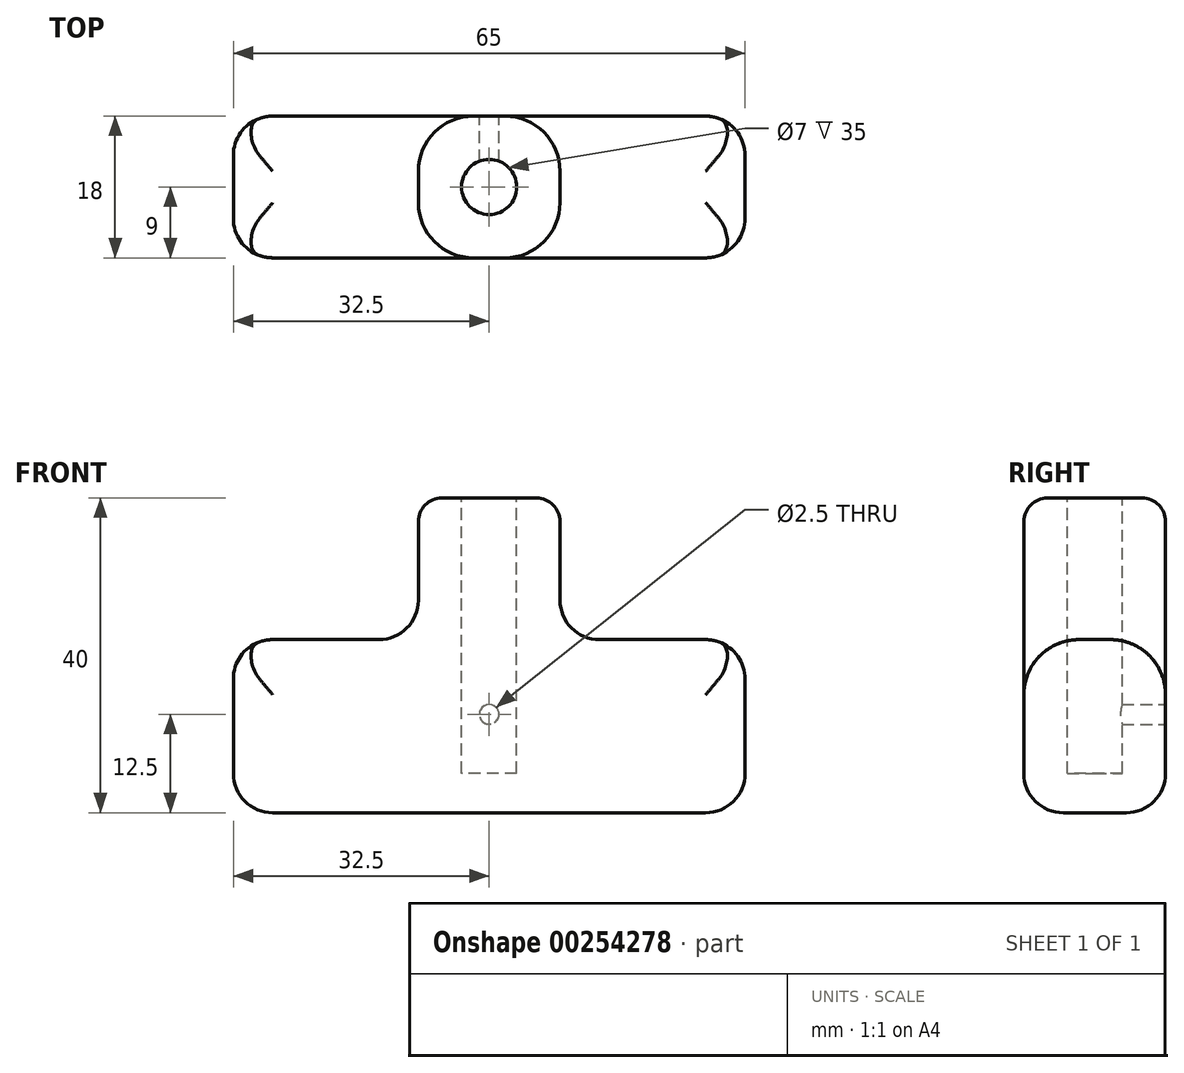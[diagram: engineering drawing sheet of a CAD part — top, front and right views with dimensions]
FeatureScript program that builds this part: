
annotation { "Feature Type Name" : "Feature", "Feature Type Description" : "" }
export const myFeature = defineFeature(function(context is Context, id is Id, definition is map)
    precondition{}
    {
        {
            var Q0;
            Q0=qCreatedBy(makeId("Front.planeOp"),FACE);
            var sketch = newSketch(context, id + "F0", { "sketchPlane" : qUnion([Q0])});
            skLineSegment(sketch, "E0", {"start": v(0, 0) * mm, "end": v(0, 40) * mm, "construction": true});
            skLineSegment(sketch, "E1", {"start": v(0, 0) * mm, "end": v(32.5, 0) * mm});
            skLineSegment(sketch, "E2", {"start": v(32.5, 0) * mm, "end": v(32.5, 22) * mm});
            skLineSegment(sketch, "E3", {"start": v(32.5, 22) * mm, "end": v(9, 22) * mm});
            skLineSegment(sketch, "E4", {"start": v(9, 22) * mm, "end": v(9, 40) * mm});
            skLineSegment(sketch, "E5", {"start": v(9, 40) * mm, "end": v(0, 40) * mm});
            skLineSegment(sketch, "E6.MirrorCS", {"start": v(-9, 40) * mm, "end": v(0, 40) * mm});
            skLineSegment(sketch, "E7.MirrorCS", {"start": v(-9, 22) * mm, "end": v(-9, 40) * mm});
            skLineSegment(sketch, "E8.MirrorCS", {"start": v(-32.5, 22) * mm, "end": v(-9, 22) * mm});
            skLineSegment(sketch, "E9.MirrorCS", {"start": v(-32.5, 0) * mm, "end": v(-32.5, 22) * mm});
            skLineSegment(sketch, "E10.MirrorCS", {"start": v(0, 0) * mm, "end": v(-32.5, 0) * mm});
            skSolve(sketch);
        }
        {
            var Q0;
            Q0=makeQuery(id+"F0.imprint","IMPRINT",FACE,{"disambiguationData":[TD([[makeQuery(id+"F0.imprint","IMPRINT",EDGE,{"derivedFrom":sQuery(id+"F0.wireOp",EDGE,"E1")}),1.0]])]});
            extrude(context, id + "F1", {"entities" : qUnion([Q0]), "depth" : 18 * mm, "offsetDistance" : 25 * mm, "symmetric" : true});
        }
        {
            var Q0;
            Q0=makeQuery(id+"F1.opExtrude","SWEPT_FACE",FACE,{"disambiguationData":[OSD([sQuery(id+"F0.wireOp",EDGE,"E5"),sQuery(id+"F0.wireOp",EDGE,"E6.MirrorCS")])]});
            var sketch = newSketch(context, id + "F2", { "sketchPlane" : qUnion([Q0])});
            skPoint(sketch, "E11.0", {"position": v(0, 0) * mm});
            skCircle(sketch, "E12", {"center": v(0, 0) * mm, "radius": 3.5 * mm});
            skSolve(sketch);
        }
        {
            var Q0;
            Q0=makeQuery(id+"F2.imprint","IMPRINT",FACE,{"disambiguationData":[TD([[makeQuery(id+"F2.imprint","IMPRINT",EDGE,{"derivedFrom":sQuery(id+"F2.wireOp",EDGE,"E12")}),1.0]])]});
            extrude(context, id + "F3", {"entities" : qUnion([Q0]), "operationType" : NewBodyOperationType.REMOVE, "oppositeDirection" : true, "depth" : 35 * mm, "offsetDistance" : 25 * mm});
        }
        {
            var Q0;
            Q0=makeQuery(id+"F1.opExtrude","CAP_EDGE",EDGE,{"disambiguationData":[OSD([sQuery(id+"F0.wireOp",EDGE,"E8.MirrorCS")])],"isStart":false});
            var Q1;
            Q1=makeQuery(id+"F1.opExtrude","CAP_EDGE",EDGE,{"disambiguationData":[OSD([sQuery(id+"F0.wireOp",EDGE,"E8.MirrorCS")])],"isStart":true});
            var Q2;
            Q2=makeQuery(id+"F1.opExtrude","CAP_EDGE",EDGE,{"disambiguationData":[OSD([sQuery(id+"F0.wireOp",EDGE,"E3")])],"isStart":false});
            var Q3;
            Q3=makeQuery(id+"F1.opExtrude","CAP_EDGE",EDGE,{"disambiguationData":[OSD([sQuery(id+"F0.wireOp",EDGE,"E3")])],"isStart":true});
            var Q4;
            Q4=makeQuery(id+"F1.opExtrude","CAP_EDGE",EDGE,{"disambiguationData":[OSD([sQuery(id+"F0.wireOp",EDGE,"E1"),sQuery(id+"F0.wireOp",EDGE,"E10.MirrorCS")])],"isStart":false});
            var Q5;
            Q5=makeQuery(id+"F1.opExtrude","CAP_EDGE",EDGE,{"disambiguationData":[OSD([sQuery(id+"F0.wireOp",EDGE,"E1"),sQuery(id+"F0.wireOp",EDGE,"E10.MirrorCS")])],"isStart":true});
            fillet(context, id + "F4", {"entities" : qUnion([Q0, Q1, Q2, Q3, Q4, Q5]), "tangentPropagation" : true, "radius" : 5 * mm, "defaultsChanged" : true, "vertexSettings" : [], "allowEdgeOverflow" : false});
        }
        {
            var Q0;
            Q0=makeQuery(id+"F1.opExtrude","CAP_EDGE",EDGE,{"disambiguationData":[OSD([sQuery(id+"F0.wireOp",EDGE,"E9.MirrorCS")])],"isStart":true});
            var Q1;
            Q1=makeQuery(id+"F1.opExtrude","CAP_EDGE",EDGE,{"disambiguationData":[OSD([sQuery(id+"F0.wireOp",EDGE,"E2")])],"isStart":true});
            var Q2;
            Q2=makeQuery(id+"F1.opExtrude","SWEPT_EDGE",EDGE,{"disambiguationData":[OSD([sQuery(id+"F0.wireOp",EDGE,"E3"),sQuery(id+"F0.wireOp",EDGE,"E4")])]});
            var Q3;
            Q3=makeQuery(id+"F1.opExtrude","SWEPT_EDGE",EDGE,{"disambiguationData":[OSD([sQuery(id+"F0.wireOp",EDGE,"E7.MirrorCS"),sQuery(id+"F0.wireOp",EDGE,"E8.MirrorCS")])]});
            fillet(context, id + "F5", {"entities" : qUnion([Q0, Q1, Q2, Q3]), "tangentPropagation" : true, "radius" : 5 * mm, "defaultsChanged" : false, "vertexSettings" : [], "allowEdgeOverflow" : false});
        }
        {
            var Q0;
            Q0=makeQuery(id+"F1.opExtrude","CAP_EDGE",EDGE,{"disambiguationData":[OSD([sQuery(id+"F0.wireOp",EDGE,"E4")])],"isStart":true});
            var Q1;
            Q1=makeQuery(id+"F1.opExtrude","CAP_EDGE",EDGE,{"disambiguationData":[OSD([sQuery(id+"F0.wireOp",EDGE,"E4")])],"isStart":false});
            var Q2;
            Q2=makeQuery(id+"F1.opExtrude","CAP_EDGE",EDGE,{"disambiguationData":[OSD([sQuery(id+"F0.wireOp",EDGE,"E7.MirrorCS")])],"isStart":true});
            var Q3;
            Q3=makeQuery(id+"F1.opExtrude","CAP_EDGE",EDGE,{"disambiguationData":[OSD([sQuery(id+"F0.wireOp",EDGE,"E7.MirrorCS")])],"isStart":false});
            fillet(context, id + "F6", {"entities" : qUnion([Q0, Q1, Q2, Q3]), "tangentPropagation" : true, "radius" : 7 * mm, "defaultsChanged" : true, "vertexSettings" : [], "allowEdgeOverflow" : false});
        }
        {
            var Q0;
            Q0=makeQuery(id+"F6.opFillet","BLEND_EDGE",EDGE,{"blendedFrom":[makeQuery(id+"F1.opExtrude","CAP_EDGE",EDGE,{"disambiguationData":[OSD([sQuery(id+"F0.wireOp",EDGE,"E7.MirrorCS")])],"isStart":true}),makeQuery(id+"F1.opExtrude","SWEPT_FACE",FACE,{"disambiguationData":[OSD([sQuery(id+"F0.wireOp",EDGE,"E5"),sQuery(id+"F0.wireOp",EDGE,"E6.MirrorCS")])]})],"blendedInto":[makeQuery(id+"F1.opExtrude","SWEPT_FACE",FACE,{"disambiguationData":[OSD([sQuery(id+"F0.wireOp",EDGE,"E5"),sQuery(id+"F0.wireOp",EDGE,"E6.MirrorCS")])]})]});
            fillet(context, id + "F7", {"entities" : qUnion([Q0]), "tangentPropagation" : true, "radius" : 3 * mm, "defaultsChanged" : true, "vertexSettings" : [], "allowEdgeOverflow" : false});
        }
        {
            var Q0;
            Q0=makeQuery(id+"F1.opExtrude","CAP_FACE",FACE,{"disambiguationData":[OSD([sQuery(id+"F0.wireOp",EDGE,"E1"),sQuery(id+"F0.wireOp",EDGE,"E2"),sQuery(id+"F0.wireOp",EDGE,"E3"),sQuery(id+"F0.wireOp",EDGE,"E4"),sQuery(id+"F0.wireOp",EDGE,"E5"),sQuery(id+"F0.wireOp",EDGE,"E6.MirrorCS"),sQuery(id+"F0.wireOp",EDGE,"E7.MirrorCS"),sQuery(id+"F0.wireOp",EDGE,"E8.MirrorCS"),sQuery(id+"F0.wireOp",EDGE,"E9.MirrorCS"),sQuery(id+"F0.wireOp",EDGE,"E10.MirrorCS")])],"isStart":true});
            var sketch = newSketch(context, id + "F8", { "sketchPlane" : qUnion([Q0])});
            skLineSegment(sketch, "E13.0", {"start": v(-3.5, 5) * mm, "end": v(3.5, 5) * mm, "construction": true});
            skCircle(sketch, "E14", {"center": v(0, 12.5) * mm, "radius": 1.25 * mm});
            skPoint(sketch, "E14.centerSnap0", {"position": v(0, 5) * mm});
            skSolve(sketch);
        }
        {
            var Q0;
            Q0=makeQuery(id+"F8.imprint","IMPRINT",FACE,{"disambiguationData":[TD([[makeQuery(id+"F8.imprint","IMPRINT",EDGE,{"derivedFrom":sQuery(id+"F8.wireOp",EDGE,"E14")}),1.0]])]});
            extrude(context, id + "F9", {"entities" : qUnion([Q0]), "operationType" : NewBodyOperationType.REMOVE, "endBound" : BoundingType.UP_TO_NEXT, "oppositeDirection" : true, "depth" : 25 * mm, "offsetDistance" : 25 * mm});
        }
    });
